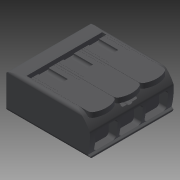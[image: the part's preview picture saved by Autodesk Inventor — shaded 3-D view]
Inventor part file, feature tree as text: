
AUTODESK INVENTOR PART (.ipt)
format: ipt  version: 2018 (Build 220112000, 112)  size: 336,896 bytes
history: native  units: mm
features: extrude x16, sketch x9, other x7
ambient origin geometry x8: Origin, YZ Plane, XZ Plane, XY Plane, X Axis, Y Axis, Z Axis, Center Point
bodies: Solid1 (feature_tree)
feature tree (32):
  extrude  "Extrusion1"  Depth=18.6mm TaperAngle=0.0deg
  extrude  "Extrusion2"  Depth=2.0mm TaperAngle=0.0deg
  extrude  "Extrusion3"  Depth=2.0mm TaperAngle=0.0deg
  other  "Pattern_1_SKETCH_1"
  other  "Pattern_1_SKETCH_2"
  extrude  "Extrusion4"  Depth=14.98mm TaperAngle=0.0deg
  extrude  "Extrusion5"  Depth=1.1mm TaperAngle=0.0deg
  extrude  "Extrusion6"  Depth=1.1mm TaperAngle=0.0deg
  extrude  "Extrusion7"  Depth=5.2mm TaperAngle=0.0deg
  extrude  "Extrusion8"  Depth=16.8mm TaperAngle=0.0deg
  extrude  "Extrusion9"  [1 undecoded]
  extrude  "Extrusion10"  [1 undecoded]
  other  "Pattern_3_SKETCH_1"
  other  "Pattern_3_SKETCH_2"
  extrude  "Extrusion11"  [1 undecoded]
  extrude  "Extrusion12"  [1 undecoded]
  extrude  "Extrusion13"  [1 undecoded]
  other  "Pattern_4_SKETCH_1"
  other  "Pattern_4_SKETCH_2"
  extrude  "Extrusion14"  [1 undecoded]
  extrude  "Extrusion15"  [1 undecoded]
  extrude  "Extrusion16"  [1 undecoded]
  sketch  "Sketch_1"  dims[d0=18.6mm d1=0.0mm d2=18.6mm d3=0.0mm]
  sketch  "Sketch_5"  dims[d12=14.98mm d13=0.0mm d14=14.98mm d15=0.0mm]
  sketch  "Sketch_2"  dims[d4=2.0mm d5=0.0mm d6=2.0mm d7=0.0mm]
  sketch  "Sketch_4"  dims[d8=2.0mm d9=0.0mm d10=2.0mm d11=0.0mm]
  sketch  "Sketch_6"  dims[d16=14.98mm d17=0.0mm d18=1.1mm d19=0.0mm]
  other  "Pattern_2_SKETCH_1"
  sketch  "Sketch_13"
  sketch  "Sketch_8"  dims[d20=1.1mm d21=0.0mm d22=1.1mm d23=0.0mm]
  sketch  "Sketch_10"  dims[d24=5.2mm d25=0.0mm d26=5.2mm d27=0.0mm]
  sketch  "Sketch_12"  dims[d28=5.2mm d29=0.0mm d30=16.8mm d31=0.0mm]
note: 8 required parameter values undecoded (feature->parameter linkage not recoverable at this tier; creation-order binding heuristic only, values carry confidence <= 0.55)
